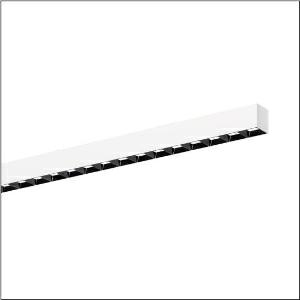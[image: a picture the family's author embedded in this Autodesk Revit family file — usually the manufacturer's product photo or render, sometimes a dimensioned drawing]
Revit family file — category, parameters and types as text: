
# Revit family: silica_r__21_51mx21tctaw_c13c
name_source: partatom
category: Lighting Fixtures
units: mm (PartAtom-declared; Revit-internal decimal feet)

## family parameters
Cut with Voids When Loaded = No
Host = Face
Light Source = No
Part Type = Normal
Room Calculation Point = No
Round Connector Dimension = Use Diameter
Shared = No

## types (1)
- --- (1 x LED, 9300 lm, 80.5 W, 6500K)
    Apparent Load = 81 VA
    CIE Flux Codes = 85 99 100 100 100
    Color Rendering = 80
    Color Temperature = 6500K
    Default Elevation = 1800 mm
    Description = Silica® 21, office luminaire, primary light control with darklight reflector, of PMMA, black, CAT 2 (L<= 3000cd/m²), light emission: direct distribution, primary light characteristic: symmetric, installation type: surface-mounted, LED, rated luminous flux: 9.300lm, luminous efficacy: 110lm/W, light colour: 8tw, colour temperature: 2700..6500K, control gear: ECG DALI, with terminal, 3+2-pole, max. 2.5mm², mains connection: 220..240V, AC, 50/60Hz, rated input power: 84.6W, luminaire housing, of aluminium, traffic white (RAL 9016), length: 3.004mm, width: 53mm, height: 53mm, protection rating (complete): IP20, insulation class (complete): insulation class I (protective earthing), certification: CE, permissible operating ambient temperature: 0..+35°C, standard: EN 50419, packaging unit: 1 piece
    Height = 0 mm  [stored 0 ft]
    Lamp = 1 x LED
    Lamp Light Flux = 9300 lm
    Lamp Power = 80.5 W
    Lamp count = 1
    Length = 3004 mm
    Luminous efficacy = 116 lm/W
    Manufacturer = Siteco
    ModVariant = No
    Model = 51MX21TCTAW
    Mounting Place = Ceiling
    Mounting Type = Recessed
    Number of Poles = 1
    OnlyDefault = Yes
    Power Factor = 1
    Product Name = Silica® 21
    Product group = office luminaire | ceiling recessed
    ProductGroupID = 401
    Protection Class = Protection class I
    Protection Degree = IP 20
    RLX_Detail_Level = 1
    RLX_Emergency_Light_Flux = 0 lm
    RLX_Emergency_Type = 0
    RLX_Emergency_Type_DB = No
    RlxData = <blob elided: 58685 chars, md5=f8f0a86a>
    Socket = socket
    Standby Power = 0 W
    System Light Flux = 9300 lm
    System Power = 81 W
    Type Comments = individual setting
    Type Image = l_1313592.jpg
    URL = http://relux.com
    VarID = @adj_089445
    Voltage = 0 V
    Weight = 0.00 kg
    Width = 53 mm

note: [stored X ft] marks values corroborated as IEEE doubles in the binary element streams (Revit-internal decimal feet)

## geometry (parser evidence)
native form markers: Blend x4, Sweep x10
no freeform markers — native parametric forms only
